# Revit family: CL60024-B_ROUND TOILET ROLL HOLDER WITH SHELF
name_source: partatom
category: Specialty Equipment
revit_build: Autodesk Revit 2015 (Build: 20140606_1530(x64)
units: mm (PartAtom-declared; Revit-internal decimal feet)

## types (3) — shared parameters
Assembly Code = C1030200
Default Elevation = 900 mm  [stored 2.95276 ft]
Manufacturer = GWA Bathrooms & Kitchens
URL = https://www.clark.com.au

## per-type parameters (varying)
| type | Material_Base | Model |
| ROUND TOILET ROLL HOLDER WITH SHELF CHROME | GWA_Metal-Chrome | CL60024.C |
| ROUND TOILET ROLL HOLDER WITH SHELF BLACK | GWA-Metal-Black | CL60024.B |
| ROUND TOILET ROLL HOLDER WITH SHELF WHITE | GWA-Metal-White | CL60024.W |

note: column(s) folded — value = type name in every type: Description

note: [stored X ft] marks values corroborated as IEEE doubles in the binary element streams (Revit-internal decimal feet)

## geometry (parser evidence)
native form markers: Sweep x2
no freeform markers — native parametric forms only
